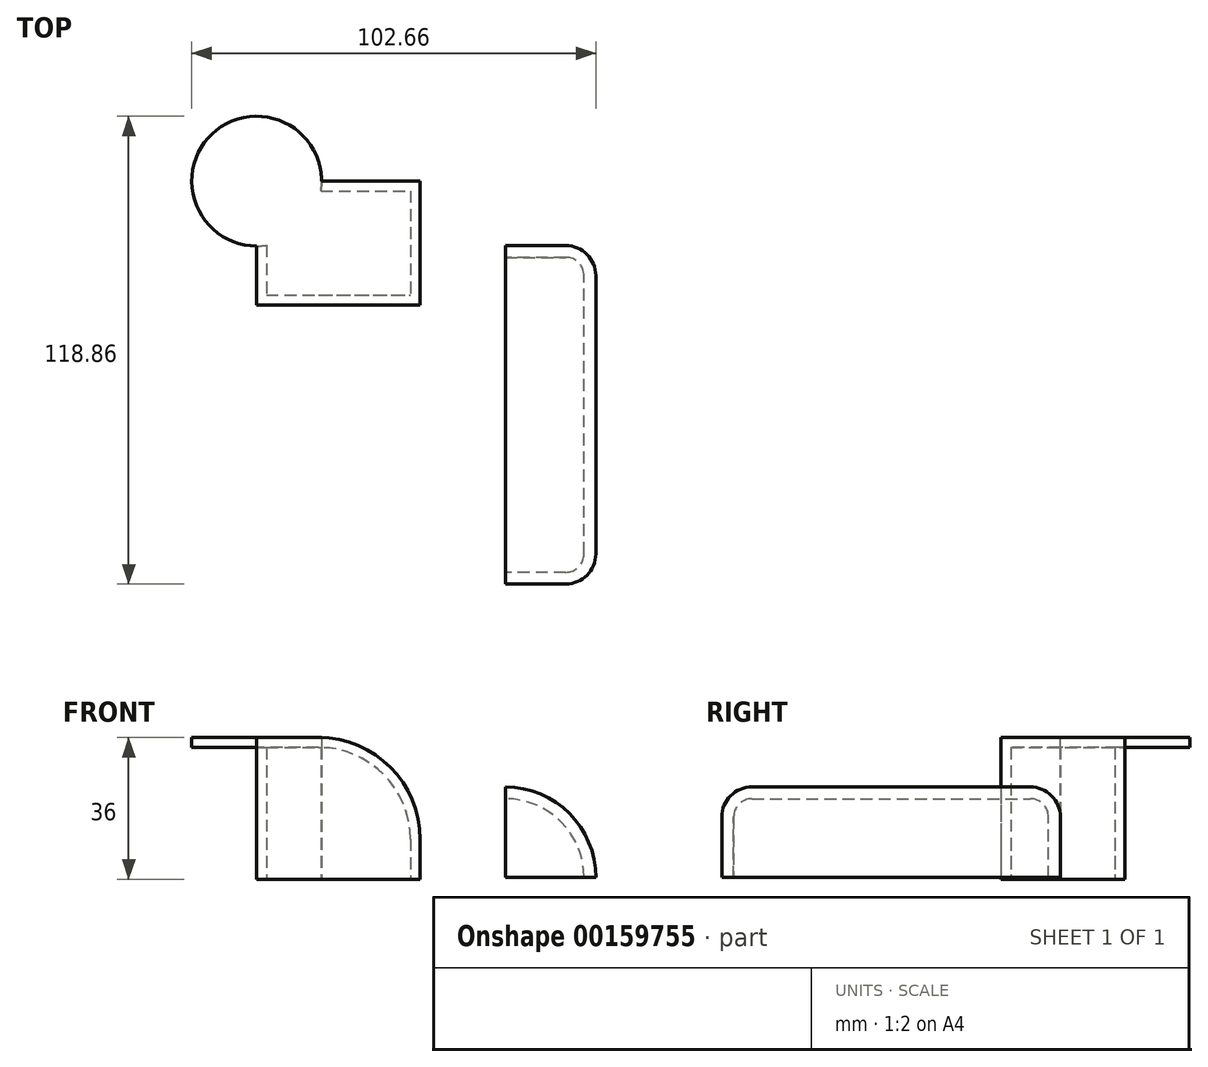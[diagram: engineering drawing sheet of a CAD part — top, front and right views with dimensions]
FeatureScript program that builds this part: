
annotation { "Feature Type Name" : "Feature", "Feature Type Description" : "" }
export const myFeature = defineFeature(function(context is Context, id is Id, definition is map)
    precondition{}
    {
        {
            var Q0;
            Q0=qCreatedBy(makeId("Right.planeOp"),FACE);
            var sketch = newSketch(context, id + "F0", { "sketchPlane" : qUnion([Q0])});
            skLineSegment(sketch, "E0.top", {"start": v(-52.74, 20.46) * mm, "end": v(17.95, 20.46) * mm});
            skLineSegment(sketch, "E0.left", {"start": v(-57.4, 5.11) * mm, "end": v(-57.4, 15.8) * mm});
            skLineSegment(sketch, "E0.right", {"start": v(22.6, 5.11) * mm, "end": v(22.6, 15.8) * mm});
            skPoint(sketch, "E1.visualSharp", {"position": v(-57.4, 20.46) * mm});
            skArc(sketch, "E1.filletArc", {"start": v(-52.74, 20.46) * mm, "mid": v(-56.03, 19.1) * mm, "end": v(-57.4, 15.8) * mm});
            skPoint(sketch, "E2.visualSharp", {"position": v(22.6, 20.46) * mm});
            skArc(sketch, "E2.filletArc", {"start": v(22.6, 15.8) * mm, "mid": v(21.24, 19.1) * mm, "end": v(17.95, 20.46) * mm});
            skPoint(sketch, "E3.visualSharp", {"position": v(22.6, 0.46) * mm});
            skPoint(sketch, "E4.visualSharp", {"position": v(-57.4, 0.46) * mm});
            skLineSegment(sketch, "E5", {"start": v(-57.4, 5.11) * mm, "end": v(-57.4, 0.46) * mm});
            skLineSegment(sketch, "E6", {"start": v(-57.4, 0.46) * mm, "end": v(-60.62, 0.46) * mm});
            skLineSegment(sketch, "E7", {"start": v(22.6, 5.11) * mm, "end": v(22.6, 0.46) * mm});
            skLineSegment(sketch, "E8.0", {"start": v(25.6, 5.11) * mm, "end": v(25.6, 0.46) * mm});
            skLineSegment(sketch, "E8.1", {"start": v(25.6, 5.11) * mm, "end": v(25.6, 15.8) * mm});
            skArc(sketch, "E8.2", {"start": v(25.6, 15.8) * mm, "mid": v(23.36, 21.21) * mm, "end": v(17.95, 23.46) * mm});
            skLineSegment(sketch, "E8.3", {"start": v(-60.4, 5.11) * mm, "end": v(-60.4, 0.46) * mm});
            skLineSegment(sketch, "E8.4", {"start": v(-60.4, 5.11) * mm, "end": v(-60.4, 15.8) * mm});
            skArc(sketch, "E8.5", {"start": v(-52.74, 23.46) * mm, "mid": v(-58.15, 21.21) * mm, "end": v(-60.4, 15.8) * mm});
            skLineSegment(sketch, "E8.6", {"start": v(-52.74, 23.46) * mm, "end": v(17.95, 23.46) * mm});
            skLineSegment(sketch, "E9", {"start": v(22.6, 0.46) * mm, "end": v(25.6, 0.46) * mm});
            skSolve(sketch);
        }
        {
            var Q0;
            Q0 = qSketchRegion(id + "F0", true);
            var Q1;
            Q1=sQuery(id+"F0.wireOp",EDGE,"E6");
            revolve(context, id + "F1", {"entities" : qUnion([Q0]), "axis" : qUnion([Q1]), "revolveType" : RevolveType.ONE_DIRECTION, "oppositeDirection" : true, "angle" : 90 * degree});
        }
        {
            var Q0;
            Q0=qCreatedBy(makeId("Top.planeOp"),FACE);
            var sketch = newSketch(context, id + "F2", { "sketchPlane" : qUnion([Q0])});
            skLineSegment(sketch, "E10.bottom", {"start": v(-46.68, 41.97) * mm, "end": v(-21.62, 41.97) * mm});
            skLineSegment(sketch, "E10.top", {"start": v(-63.17, 10.53) * mm, "end": v(-21.62, 10.53) * mm});
            skLineSegment(sketch, "E10.left", {"start": v(-63.17, 25.48) * mm, "end": v(-63.17, 10.53) * mm});
            skLineSegment(sketch, "E10.right", {"start": v(-21.62, 41.97) * mm, "end": v(-21.62, 10.53) * mm});
            skArc(sketch, "E11", {"start": v(-46.68, 41.97) * mm, "mid": v(-74.83, 53.63) * mm, "end": v(-63.17, 25.48) * mm});
            skSolve(sketch);
        }
        {
            var Q0;
            Q0=makeQuery(id+"F2.imprint","IMPRINT",FACE,{"disambiguationData":[TD([[makeQuery(id+"F2.imprint","IMPRINT",EDGE,{"derivedFrom":sQuery(id+"F2.wireOp",EDGE,"E10.bottom")}),-1.0]])]});
            extrude(context, id + "F3", {"entities" : qUnion([Q0]), "depth" : 36 * mm});
        }
        {
            var Q0;
            Q0=makeQuery(id+"F3.opExtrude","CAP_EDGE",EDGE,{"disambiguationData":[OSD([sQuery(id+"F2.wireOp",EDGE,"E10.right")])],"isStart":false});
            fillet(context, id + "F4", {"entities" : qUnion([Q0]), "radius" : 25.83 * mm, "tangentPropagation" : true, "allowEdgeOverflow" : false});
        }
        {
            var Q0;
            Q0=makeQuery(id+"F3.opExtrude","SWEPT_FACE",FACE,{"disambiguationData":[OSD([sQuery(id+"F2.wireOp",EDGE,"E11")])]});
            var Q1;
            Q1=makeQuery(id+"F3.opExtrude","CAP_FACE",FACE,{"disambiguationData":[OSD([sQuery(id+"F2.wireOp",EDGE,"E10.bottom"),sQuery(id+"F2.wireOp",EDGE,"E10.top"),sQuery(id+"F2.wireOp",EDGE,"E10.left"),sQuery(id+"F2.wireOp",EDGE,"E10.right"),sQuery(id+"F2.wireOp",EDGE,"E11")])],"isStart":true});
            shell(context, id + "F5", {"entities" : qUnion([Q0, Q1]), "thickness" : 2.5 * mm});
        }
    });
